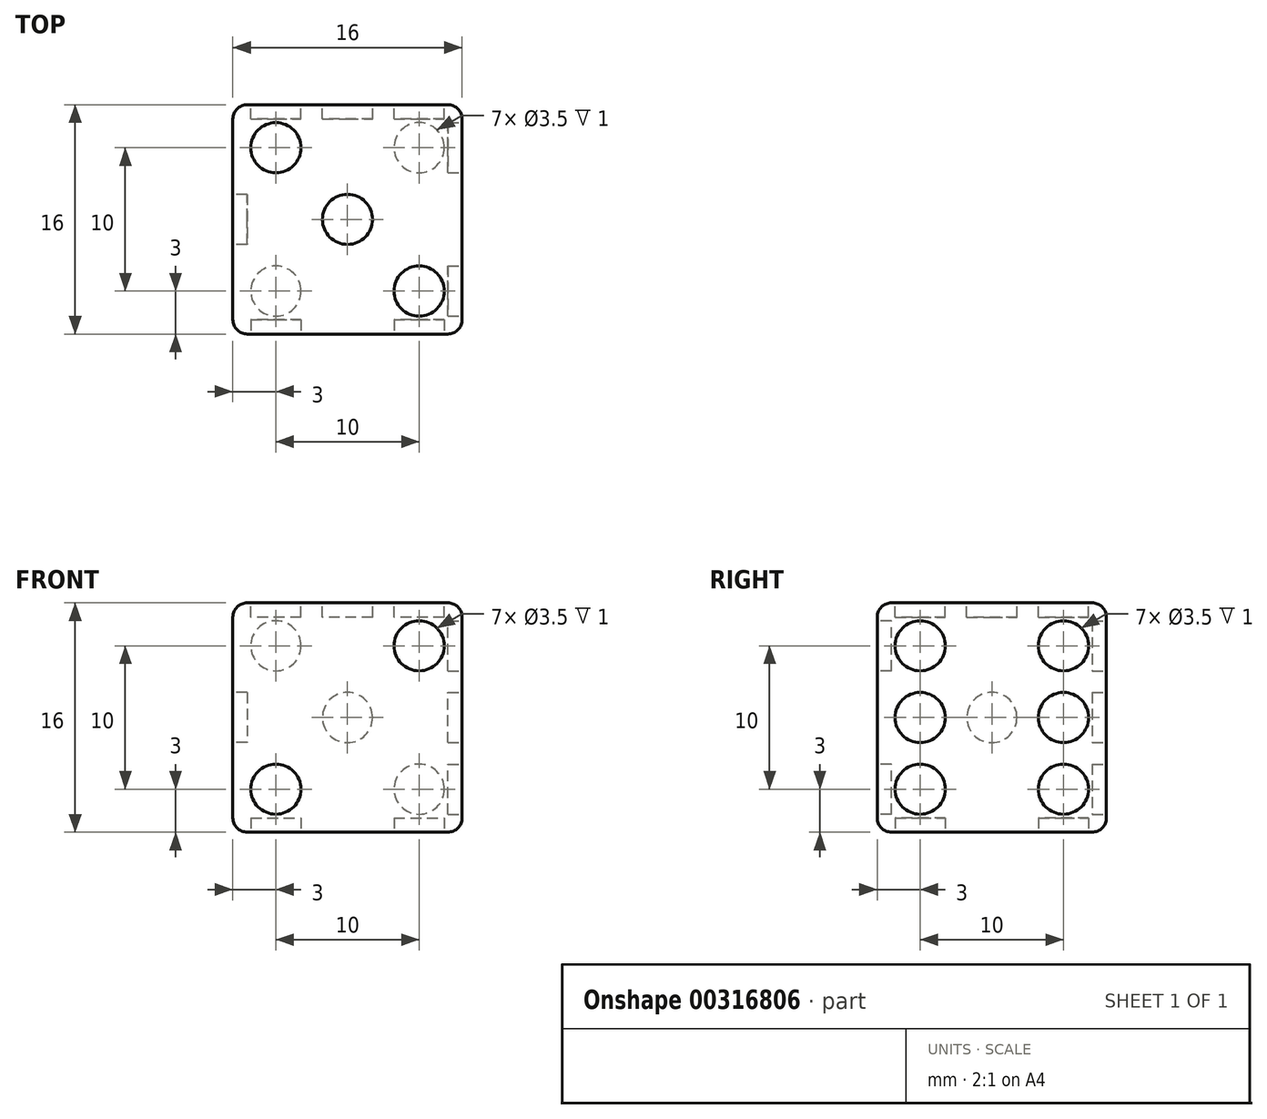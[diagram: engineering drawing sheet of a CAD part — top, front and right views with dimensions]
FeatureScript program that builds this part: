
annotation { "Feature Type Name" : "Feature", "Feature Type Description" : "" }
export const myFeature = defineFeature(function(context is Context, id is Id, definition is map)
    precondition{}
    {
        {
            var Q0;
            Q0=qCreatedBy(makeId("Front.planeOp"),FACE);
            var sketch = newSketch(context, id + "F0", { "sketchPlane" : qUnion([Q0])});
            skLineSegment(sketch, "E0.bottom", {"start": v(-8, 8) * mm, "end": v(8, 8) * mm});
            skLineSegment(sketch, "E0.top", {"start": v(-8, -8) * mm, "end": v(8, -8) * mm});
            skLineSegment(sketch, "E0.left", {"start": v(-8, 8) * mm, "end": v(-8, -8) * mm});
            skLineSegment(sketch, "E0.right", {"start": v(8, 8) * mm, "end": v(8, -8) * mm});
            skPoint(sketch, "E0.middle", {"position": v(0, 0) * mm});
            skSolve(sketch);
        }
        {
            var Q0;
            Q0 = qSketchRegion(id + "F0", true);
            extrude(context, id + "F1", {"entities" : qUnion([Q0]), "endBound" : BoundingType.SYMMETRIC, "depth" : 16 * mm});
        }
        {
            var Q0;
            Q0=makeQuery(id+"F1.opExtrude","CAP_FACE",FACE,{"disambiguationData":[OSD([sQuery(id+"F0.wireOp",EDGE,"E0.bottom"),sQuery(id+"F0.wireOp",EDGE,"E0.top"),sQuery(id+"F0.wireOp",EDGE,"E0.left"),sQuery(id+"F0.wireOp",EDGE,"E0.right")])],"isStart":false});
            var sketch = newSketch(context, id + "F2", { "sketchPlane" : qUnion([Q0])});
            skCircle(sketch, "E1", {"center": v(5, 5) * mm, "radius": 1.75 * mm});
            skCircle(sketch, "E2", {"center": v(-5, -5) * mm, "radius": 1.75 * mm});
            skSolve(sketch);
        }
        {
            var Q0;
            Q0 = qSketchRegion(id + "F2", true);
            extrude(context, id + "F3", {"entities" : qUnion([Q0]), "operationType" : NewBodyOperationType.REMOVE, "oppositeDirection" : true, "depth" : 1 * mm});
        }
        {
            var Q0;
            Q0=makeQuery(id+"F1.opExtrude","SWEPT_FACE",FACE,{"disambiguationData":[OSD([sQuery(id+"F0.wireOp",EDGE,"E0.right")])]});
            var sketch = newSketch(context, id + "F4", { "sketchPlane" : qUnion([Q0])});
            skCircle(sketch, "E3", {"center": v(-5, 5) * mm, "radius": 1.75 * mm});
            skCircle(sketch, "E4", {"center": v(-5, 0) * mm, "radius": 1.75 * mm});
            skCircle(sketch, "E5", {"center": v(-5, -5) * mm, "radius": 1.75 * mm});
            skCircle(sketch, "E6", {"center": v(5, 5) * mm, "radius": 1.75 * mm});
            skCircle(sketch, "E7", {"center": v(5, 0) * mm, "radius": 1.75 * mm});
            skCircle(sketch, "E8", {"center": v(5, -5) * mm, "radius": 1.75 * mm});
            skSolve(sketch);
        }
        {
            var Q0;
            Q0 = qSketchRegion(id + "F4", true);
            extrude(context, id + "F5", {"entities" : qUnion([Q0]), "operationType" : NewBodyOperationType.REMOVE, "oppositeDirection" : true, "depth" : 1 * mm});
        }
        {
            var Q0;
            Q0=makeQuery(id+"F1.opExtrude","SWEPT_FACE",FACE,{"disambiguationData":[OSD([sQuery(id+"F0.wireOp",EDGE,"E0.bottom")])]});
            var sketch = newSketch(context, id + "F6", { "sketchPlane" : qUnion([Q0])});
            skCircle(sketch, "E9", {"center": v(-5, 5) * mm, "radius": 1.75 * mm});
            skCircle(sketch, "E10", {"center": v(5, -5) * mm, "radius": 1.75 * mm});
            skCircle(sketch, "E11", {"center": v(0, 0) * mm, "radius": 1.75 * mm});
            skSolve(sketch);
        }
        {
            var Q0;
            Q0 = qSketchRegion(id + "F6", true);
            extrude(context, id + "F7", {"entities" : qUnion([Q0]), "operationType" : NewBodyOperationType.REMOVE, "oppositeDirection" : true, "depth" : 1 * mm});
        }
        {
            var Q0;
            Q0=makeQuery(id+"F1.opExtrude","CAP_EDGE",EDGE,{"disambiguationData":[OSD([sQuery(id+"F0.wireOp",EDGE,"E0.bottom")])],"isStart":false});
            var Q1;
            Q1=makeQuery(id+"F1.opExtrude","SWEPT_EDGE",EDGE,{"disambiguationData":[OSD([sQuery(id+"F0.wireOp",EDGE,"E0.bottom"),sQuery(id+"F0.wireOp",EDGE,"E0.right")])]});
            var Q2;
            Q2=makeQuery(id+"F1.opExtrude","CAP_EDGE",EDGE,{"disambiguationData":[OSD([sQuery(id+"F0.wireOp",EDGE,"E0.right")])],"isStart":false});
            var Q3;
            Q3=makeQuery(id+"F1.opExtrude","CAP_EDGE",EDGE,{"disambiguationData":[OSD([sQuery(id+"F0.wireOp",EDGE,"E0.right")])],"isStart":true});
            var Q4;
            Q4=makeQuery(id+"F1.opExtrude","SWEPT_EDGE",EDGE,{"disambiguationData":[OSD([sQuery(id+"F0.wireOp",EDGE,"E0.top"),sQuery(id+"F0.wireOp",EDGE,"E0.right")])]});
            var Q5;
            Q5=makeQuery(id+"F1.opExtrude","CAP_EDGE",EDGE,{"disambiguationData":[OSD([sQuery(id+"F0.wireOp",EDGE,"E0.bottom")])],"isStart":true});
            var Q6;
            Q6=makeQuery(id+"F1.opExtrude","SWEPT_EDGE",EDGE,{"disambiguationData":[OSD([sQuery(id+"F0.wireOp",EDGE,"E0.bottom"),sQuery(id+"F0.wireOp",EDGE,"E0.left")])]});
            var Q7;
            Q7=makeQuery(id+"F1.opExtrude","CAP_EDGE",EDGE,{"disambiguationData":[OSD([sQuery(id+"F0.wireOp",EDGE,"E0.left")])],"isStart":true});
            var Q8;
            Q8=makeQuery(id+"F1.opExtrude","CAP_EDGE",EDGE,{"disambiguationData":[OSD([sQuery(id+"F0.wireOp",EDGE,"E0.top")])],"isStart":true});
            var Q9;
            Q9=makeQuery(id+"F1.opExtrude","SWEPT_EDGE",EDGE,{"disambiguationData":[OSD([sQuery(id+"F0.wireOp",EDGE,"E0.top"),sQuery(id+"F0.wireOp",EDGE,"E0.left")])]});
            var Q10;
            Q10=makeQuery(id+"F1.opExtrude","CAP_EDGE",EDGE,{"disambiguationData":[OSD([sQuery(id+"F0.wireOp",EDGE,"E0.top")])],"isStart":false});
            var Q11;
            Q11=makeQuery(id+"F1.opExtrude","CAP_EDGE",EDGE,{"disambiguationData":[OSD([sQuery(id+"F0.wireOp",EDGE,"E0.left")])],"isStart":false});
            fillet(context, id + "F8", {"entities" : qUnion([Q0, Q1, Q2, Q3, Q4, Q5, Q6, Q7, Q8, Q9, Q10, Q11]), "radius" : 1 * mm, "tangentPropagation" : true, "allowEdgeOverflow" : false});
        }
        {
            var Q0;
            Q0=makeQuery(id+"F1.opExtrude","SWEPT_FACE",FACE,{"disambiguationData":[OSD([sQuery(id+"F0.wireOp",EDGE,"E0.left")])]});
            var sketch = newSketch(context, id + "F9", { "sketchPlane" : qUnion([Q0])});
            skCircle(sketch, "E12", {"center": v(0, 0) * mm, "radius": 1.75 * mm});
            skSolve(sketch);
        }
        {
            var Q0;
            Q0 = qSketchRegion(id + "F9", true);
            extrude(context, id + "F10", {"entities" : qUnion([Q0]), "operationType" : NewBodyOperationType.REMOVE, "oppositeDirection" : true, "depth" : 1 * mm});
        }
        {
            var Q0;
            Q0=makeQuery(id+"F1.opExtrude","CAP_FACE",FACE,{"disambiguationData":[OSD([sQuery(id+"F0.wireOp",EDGE,"E0.bottom"),sQuery(id+"F0.wireOp",EDGE,"E0.top"),sQuery(id+"F0.wireOp",EDGE,"E0.left"),sQuery(id+"F0.wireOp",EDGE,"E0.right")])],"isStart":true});
            var sketch = newSketch(context, id + "F11", { "sketchPlane" : qUnion([Q0])});
            skCircle(sketch, "E13", {"center": v(-5, 5) * mm, "radius": 1.75 * mm});
            skCircle(sketch, "E14", {"center": v(-5, -5) * mm, "radius": 1.75 * mm});
            skCircle(sketch, "E15", {"center": v(5, 5) * mm, "radius": 1.75 * mm});
            skCircle(sketch, "E16", {"center": v(5, -5) * mm, "radius": 1.75 * mm});
            skCircle(sketch, "E17", {"center": v(0, 0) * mm, "radius": 1.75 * mm});
            skSolve(sketch);
        }
        {
            var Q0;
            Q0 = qSketchRegion(id + "F11", true);
            extrude(context, id + "F12", {"entities" : qUnion([Q0]), "operationType" : NewBodyOperationType.REMOVE, "oppositeDirection" : true, "depth" : 1 * mm});
        }
        {
            var Q0;
            Q0=makeQuery(id+"F1.opExtrude","SWEPT_FACE",FACE,{"disambiguationData":[OSD([sQuery(id+"F0.wireOp",EDGE,"E0.top")])]});
            var sketch = newSketch(context, id + "F13", { "sketchPlane" : qUnion([Q0])});
            skCircle(sketch, "E18", {"center": v(-5, 5) * mm, "radius": 1.75 * mm});
            skCircle(sketch, "E19", {"center": v(5, 5) * mm, "radius": 1.75 * mm});
            skCircle(sketch, "E20", {"center": v(5, -5) * mm, "radius": 1.75 * mm});
            skCircle(sketch, "E21", {"center": v(-5, -5) * mm, "radius": 1.75 * mm});
            skSolve(sketch);
        }
        {
            var Q0;
            Q0 = qSketchRegion(id + "F13", true);
            extrude(context, id + "F14", {"entities" : qUnion([Q0]), "operationType" : NewBodyOperationType.REMOVE, "oppositeDirection" : true, "depth" : 1 * mm});
        }
    });
